# Revit family: Flush_Valve-Closet-Zurn-ZER6000AV
name_source: partatom
category: Plumbing Fixtures
revit_build: Autodesk Revit Architecture 2015 (Build: 20140606_1530(x64)
units: mm (PartAtom-declared; Revit-internal decimal feet)

## types (1)
- ZER6000AV-CPM
    ADA Compliant = Yes
    Assembly Code = D2030400
    CW Connection = Yes
    Cold Water Connection Diameter = 1"
    Cold Water Connection Radius = 1/2"
    Designation = Flush Valve
    Flow = 0 GPM
    Gallons Per Flush = 3.5 gal
    HW Connection = No
    Manufacturer = Zurn Industries, LLC
    Model = ZER6000AV-CPM
    Product Documentation Link = http://www.zurn.com
    Product data url = https://bimobject.com
    Sensor Material = Chrome-Plated Brass - Zurn - Polished
    Type Comments = 3.5 gpf/13.2 Lpf Standard Flush Water Closet Flush Valve with Chrome Plated Metal EZ-Flush
    URL = www.zurn.com
    Valve Material = Chrome-Plated Brass - Zurn - Polished
    Valve Type = Diaphragm
    Vent Connection = No
    Waste Connection = No

## geometry (parser evidence)
native form markers: Blend x50, Sweep x2
no freeform markers — native parametric forms only
